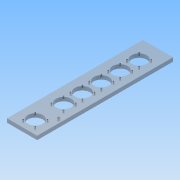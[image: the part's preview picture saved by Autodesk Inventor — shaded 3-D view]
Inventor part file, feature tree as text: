
AUTODESK INVENTOR PART (.ipt)
format: ipt  version: 2016 (Build 200138000, 138)  size: 133,632 bytes
history: native  units: mm
features: sketch x3, extrude x2, hole x2, pattern_linear x2
ambient origin geometry x8: Origin, YZ Plane, XZ Plane, XY Plane, X Axis, Y Axis, Z Axis, Center Point
bodies: Volumenkörper1 (feature_tree)
feature tree (9):
  extrude  "Extrusion1"  Depth=360.0mm
  hole  "Bohrung3"  [1 undecoded]
  extrude  "Extrusion2"  Depth=20.0mm
  hole  "Bohrung4"  [1 undecoded]
  pattern_linear  "Rechteckige Anordnung3"  Spacing1=32.0mm  [1 undecoded]
  pattern_linear  "Rechteckige Anordnung4"  Count1=5  [1 undecoded]
  sketch  "Skizze1"  dims[d0=80.0mm d1=360.0mm]
  sketch  "Skizze2"  dims[d2=10.0mm d3=0.0mm]
  sketch  "Skizze3"  dims[d31=13.0mm d32=70.0mm d33=6.0mm d34=6.0mm d35=4.0mm d36=2.0mm d37=90.0deg d38=8.0mm d39=20.594885mm d40=40.0mm d41=50.0mm d43=10.0mm d44=0.0mm d45=32.0mm d46=3.242mm d47=6.0mm d48=4.0mm d49=2.0mm d50=90.0deg d51=8.0mm d52=20.594885mm d53=50.0mm d55=50.0mm d56=20.0mm d58=275.0mm]
note: 4 required parameter values undecoded (feature->parameter linkage not recoverable at this tier; creation-order binding heuristic only, values carry confidence <= 0.55)
